# Revit family: External Light Sensor_329
name_source: partatom
category: Electrical Fixtures
revit_build: Autodesk Revit 2018 (Build: 20170223_1515(x64)
units: mm (PartAtom-declared; Revit-internal decimal feet)

## family parameters
Always vertical = Yes
Cut with Voids When Loaded = No
Maintain Annotation Orientation = No
Part Type = Normal
Room Calculation Point = No
Round Connector Dimension = Use Diameter
Shared = No
Work Plane-Based = Yes

## types (1)
- External Light Sensor
    Ambient temperature = -35°C to +70°C
    Base & mounting bracket: = Black ABS
    Cable rating = All cables must be mains rated.
    Connector type = Screw terminals:
N: DALI+
L0: DALI–
L1: No connection
    DALI : = Wire size: 1.0 mm² – 2.5 mm²
2-core solid, flexible or
stranded
Max. length: 300 m
@ 2.5 mm²
(part of DALI subnet)
    DALI consumption: = 10 mA
    Dali power supply = 13 V – 22 V
    Default Elevation = 0 mm  [stored 0 ft]
    Dimensions: = 148 mm × 82 mm × 87 mm
    EMC emission = EN 55015
    EMC immunity = EN 61547
    Environment: = Complies with WEEE and RoHS  directives.
    IP code: = IP65
    Light level reading output: = 0–200
    Light sensing angle: = When mounted vertically:
• 85° from vertical
• Horizontal plane: 360°
    Manufacturer = Helvar
    Model = 329
    Mounting angle: = Vertical (clear sensor head at top
    Mounting points: = 2 × M4 (No. 8 woodscrew)
For fixing centres, see
diagram.
    Relative humidity = Max. 90 %, noncondensing
    Safety = EN 61347-2-11
    Sensor cover: = Toughened acrylic (UV stable
    Sensor element: = Photodiode matched to
human eye response
    Socket & sensor accessory = Black glass-filled nylon
    Storage temperature = -35°C to +70°C
    Weight = 250g
    Working light range: = 1 lx – 100 000 lx

note: [stored X ft] marks values corroborated as IEEE doubles in the binary element streams (Revit-internal decimal feet)

## geometry (parser evidence)
native form markers: Sweep x2
no freeform markers — native parametric forms only
